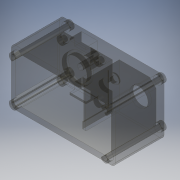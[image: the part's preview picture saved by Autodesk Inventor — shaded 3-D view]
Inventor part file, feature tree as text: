
AUTODESK INVENTOR PART (.ipt)
format: ipt  version: 2019 (Build 230136000, 136)  size: 392,704 bytes
history: native  units: mm
features: extrude x16, sketch x9, projected_geometry x3, other x3, fillet x2, reference x2
ambient origin geometry x8: Origin, YZ Plane, XZ Plane, XY Plane, X Axis, Y Axis, Z Axis, Center Point
bodies: Solid1 (feature_tree)
feature tree (35):
  sketch  "Sketch1"  dims[d0=22.75mm d1=12.2mm d2=9.0mm]
  extrude  "Extrusion1"  Depth=12.2mm
  fillet  "Fillet1"  Radius=9.0mm
  extrude  "Extrusion2"  Depth=1.0mm
  extrude  "Extrusion3"  Depth=10.5mm TaperAngle=0.0deg
  extrude  "Extrusion6"  Depth=1.0mm TaperAngle=0.0deg
  fillet  "Fillet2"  Radius=1.0mm
  sketch  "Sketch3"  dims[d6=1.75mm d7=10.5mm d8=0.0mm]
  extrude  "Extrusion7"  Depth=1.0mm
  sketch  "Sketch4"  dims[d9=1.0mm d10=1.0mm d11=0.0mm d12=1.0mm d13=0.0mm]
  extrude  "Extrusion9"  Depth=1.4mm
  extrude  "Extrusion10"  Depth=1.4mm
  extrude  "Extrusion15"  Depth=1.4mm
  extrude  "Extrusion16"  Depth=0.01mm
  sketch  "Sketch8"  dims[d19=1.4mm d20=1.4mm]
  extrude  "Extrusion17"  Depth=1.4mm
  extrude  "Extrusion18"  Depth=1.4mm
  extrude  "Extrusion19"  Depth=0.75mm
  extrude  "Extrusion20"  Depth=12.0mm
  sketch  "Sketch9"  dims[d21=1.4mm d22=1.4mm]
  extrude  "Extrusion21"  Depth=7.0mm
  extrude  "Extrusion22"  Depth=0.25mm
  extrude  "Extrusion23"  Depth=2.0mm
  sketch  "Sketch2"  dims[d3=20.0mm d4=1.0mm]
  projected_geometry  "Projected Loop1"
  sketch  "Sketch6"  dims[d15=1.2mm d16=1.0mm]
  reference  "Reference1"
  reference  "Reference2"
  sketch  "Sketch7"  dims[d17=1.4mm d18=1.4mm]
  projected_geometry  "Projected Loop2"
  sketch  "Sketch10"  dims[d27=2.0mm d28=9.0mm d29=0.0mm d30=0.0mm d31=0.01mm d32=1.4mm d33=1.4mm d34=0.75mm d35=12.0mm d36=7.0mm d37=0.25mm d38=2.0mm d39=1.025mm d40=6.5mm d41=0.0mm d44=1.0mm d45=0.0mm d46=0.75mm d47=0.75mm d48=2.0mm d49=3.5mm d50=4.75mm d51=2.0mm d52=0.0mm d59=1.25mm d60=2.5mm d65=0.25mm d66=0.0mm d67=2.0mm d68=0.0mm d69=1.15mm d70=2.0mm d71=0.5mm d72=0.0mm d73=0.25mm d74=0.0mm d75=4.0mm d77=4.75mm d78=0.75mm d79=0.0mm d80=0.75mm d81=0.0mm d82=5.0mm d83=6.0mm d84=1.0mm d85=0.0mm d86=8.0mm d89=2.75mm d90=1.75mm d91=1.0mm d92=0.0mm d93=1.0mm d94=0.0mm d95=2.25mm d96=1.15mm d97=10.75mm d98=10.0mm d99=0.0mm]
  projected_geometry  "Projected Loop3"
  other  "<userpath>\OneDrive\Documenten\Inventor\servo\Assembly1.iam"
  other  "Assembly1.iam"
  other  "sevo boven:1"
